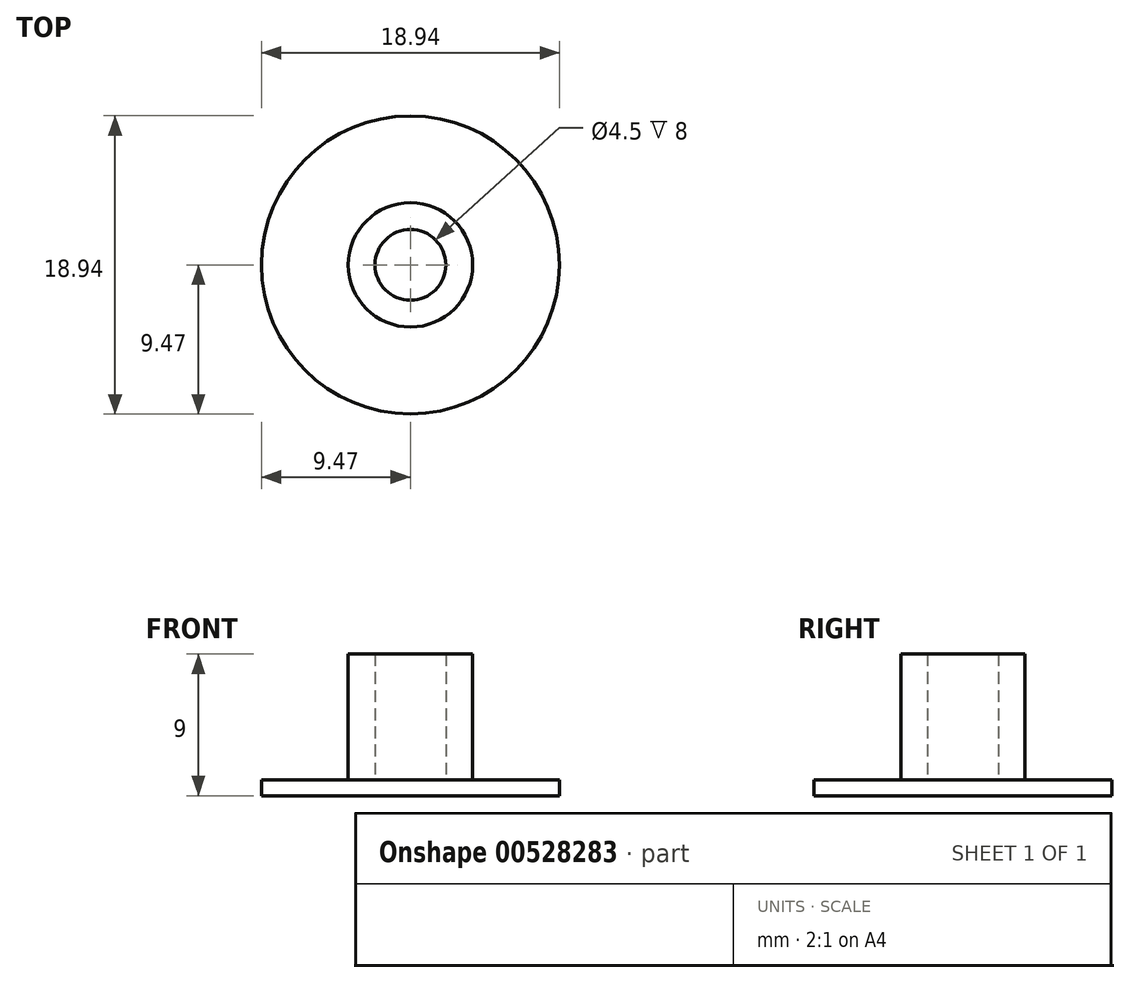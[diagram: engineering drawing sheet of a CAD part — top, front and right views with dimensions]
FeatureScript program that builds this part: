
annotation { "Feature Type Name" : "Feature", "Feature Type Description" : "" }
export const myFeature = defineFeature(function(context is Context, id is Id, definition is map)
    precondition{}
    {
        {
            var Q0;
            Q0=qCreatedBy(makeId("Top.planeOp"),FACE);
            var sketch = newSketch(context, id + "F0", { "sketchPlane" : qUnion([Q0])});
            skCircle(sketch, "E0", {"center": v(0, 0) * mm, "radius": 9.47 * mm});
            skSolve(sketch);
        }
        {
            var Q0;
            Q0=qCreatedBy(makeId("Top.planeOp"),FACE);
            var sketch = newSketch(context, id + "F1", { "sketchPlane" : qUnion([Q0])});
            skCircle(sketch, "E1", {"center": v(0, 0) * mm, "radius": 3.95 * mm});
            skSolve(sketch);
        }
        {
            var Q0;
            Q0=qCreatedBy(makeId("Top.planeOp"),FACE);
            var sketch = newSketch(context, id + "F2", { "sketchPlane" : qUnion([Q0])});
            skCircle(sketch, "E2", {"center": v(0, 0) * mm, "radius": 2.25 * mm});
            skSolve(sketch);
        }
        {
            var Q0;
            Q0 = qSketchRegion(id + "F0", true);
            extrude(context, id + "F3", {"entities" : qUnion([Q0]), "depth" : 1 * mm, "offsetDistance" : 25 * mm});
        }
        {
            var Q0;
            Q0 = qSketchRegion(id + "F1", true);
            extrude(context, id + "F4", {"entities" : qUnion([Q0]), "operationType" : NewBodyOperationType.ADD, "depth" : 9 * mm, "offsetDistance" : 25 * mm});
        }
        {
            var Q0;
            Q0=qCreatedBy(makeId("Top.planeOp"),FACE);
            var sketch = newSketch(context, id + "F5", { "sketchPlane" : qUnion([Q0])});
            skCircle(sketch, "E3", {"center": v(0, 0) * mm, "radius": 2.25 * mm});
            skSolve(sketch);
        }
        {
            var Q0;
            Q0 = qSketchRegion(id + "F2", true);
            extrude(context, id + "F6", {"entities" : qUnion([Q0]), "operationType" : NewBodyOperationType.REMOVE, "depth" : 9 * mm, "offsetDistance" : 25 * mm});
        }
        {
            var Q0;
            Q0 = qSketchRegion(id + "F5", true);
            extrude(context, id + "F7", {"entities" : qUnion([Q0]), "operationType" : NewBodyOperationType.ADD, "depth" : 1 * mm, "offsetDistance" : 25 * mm});
        }
    });
